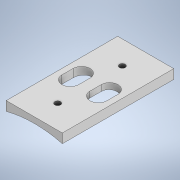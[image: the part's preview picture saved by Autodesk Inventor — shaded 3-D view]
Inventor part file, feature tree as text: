
AUTODESK INVENTOR PART (.ipt)
format: ipt  version: 2021 (Build 250183000, 183)  size: 229,376 bytes
history: native  units: in
note: dims shown in document units (in); Inventor stores cm internally (conversion verified against a paired STEP export)
features: sketch x5, extrude x4, plane x1, hole x1
ambient origin geometry x8: Origin, YZ Plane, XZ Plane, XY Plane, X Axis, Y Axis, Z Axis, Center Point
bodies: Solid1 (feature_tree)
feature tree (11):
  extrude  "Extrusion1"  Depth=0.75in
  extrude  "Extrusion2"  Depth=2.979in TaperAngle=0.0deg
  plane  "Work Plane1"
  extrude  "Extrusion3"  Depth=0.175in
  extrude  "Extrusion7"  Depth=0.75in
  hole  "Hole1"  [1 undecoded]
  sketch  "Sketch1"  dims[d0=6.0in d1=0.75in]
  sketch  "Sketch2"  dims[d2=0.5in d3=2.979in d4=0.0in]
  sketch  "Sketch4"  dims[d5=0.375in d6=0.175in]
  sketch  "Sketch20"  dims[d7=0.6in d8=0.75in]
  sketch  "Sketch21"  dims[d9=0.0in d10=0.0in d11=0.45in d12=0.75in d13=0.3in d14=0.0in d51=0.0039in d53=60.0deg d72=0.0039in d74=60.0deg d93=0.0039in d95=60.0deg d114=0.0039in d116=60.0deg d135=0.0039in d137=60.0deg d156=0.0039in d158=60.0deg d168=0.0in d169=0.0in d170=0.625in d171=0.625in d172=0.156in d173=0.38in d174=0.375in d175=0.19in d176=0.5635in d177=0.432in d178=0.8108in]
note: 1 required parameter value undecoded (feature->parameter linkage not recoverable at this tier; creation-order binding heuristic only, values carry confidence <= 0.55)
